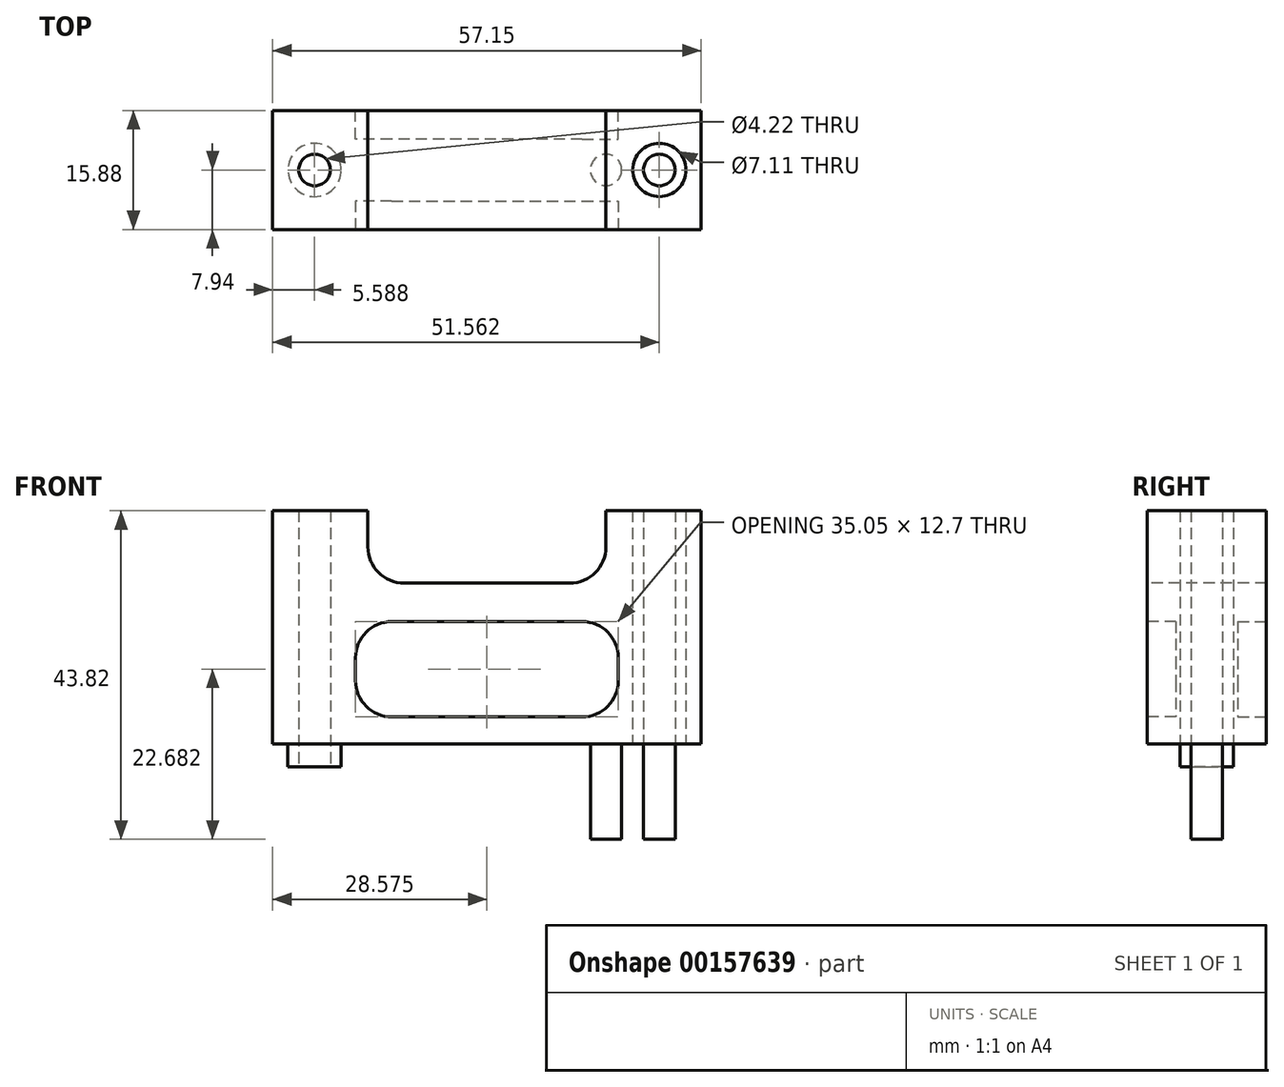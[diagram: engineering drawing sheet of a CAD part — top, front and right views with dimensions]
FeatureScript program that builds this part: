
annotation { "Feature Type Name" : "Feature", "Feature Type Description" : "" }
export const myFeature = defineFeature(function(context is Context, id is Id, definition is map)
    precondition{}
    {
        {
            var Q0;
            Q0=qCreatedBy(makeId("Right.planeOp"),FACE);
            var sketch = newSketch(context, id + "F0", { "sketchPlane" : qUnion([Q0])});
            skLineSegment(sketch, "E0", {"start": v(0, 0) * mm, "end": v(0, 11.18) * mm});
            skLineSegment(sketch, "E1", {"start": v(0, 11.18) * mm, "end": v(4.76, 11.18) * mm});
            skLineSegment(sketch, "E2", {"start": v(4.76, 11.18) * mm, "end": v(4.76, 43.82) * mm});
            skLineSegment(sketch, "E3", {"start": v(4.76, 43.82) * mm, "end": v(20.64, 43.82) * mm});
            skLineSegment(sketch, "E4", {"start": v(20.64, 43.82) * mm, "end": v(20.64, 11.18) * mm});
            skLineSegment(sketch, "E5", {"start": v(20.64, 11.18) * mm, "end": v(25.4, 11.18) * mm});
            skLineSegment(sketch, "E6", {"start": v(25.4, 11.18) * mm, "end": v(25.4, 0) * mm});
            skLineSegment(sketch, "E7", {"start": v(25.4, 0) * mm, "end": v(0, 0) * mm});
            skSolve(sketch);
        }
        {
            var Q0;
            Q0=makeQuery(id+"F0.imprint","IMPRINT",FACE,{"disambiguationData":[TD([[makeQuery(id+"F0.imprint","IMPRINT",EDGE,{"derivedFrom":sQuery(id+"F0.wireOp",EDGE,"E0")}),-1.0]])]});
            extrude(context, id + "F1", {"entities" : qUnion([Q0]), "oppositeDirection" : true, "depth" : 57.15 * mm});
        }
        {
            var Q0;
            Q0=makeQuery(id+"F1.opExtrude","SWEPT_FACE",FACE,{"disambiguationData":[OSD([sQuery(id+"F0.wireOp",EDGE,"E2")])]});
            var sketch = newSketch(context, id + "F2", { "sketchPlane" : qUnion([Q0])});
            skLineSegment(sketch, "E8", {"start": v(-44.45, 43.82) * mm, "end": v(-44.45, 38.99) * mm});
            skLineSegment(sketch, "E9", {"start": v(-39.62, 34.16) * mm, "end": v(-17.53, 34.16) * mm});
            skLineSegment(sketch, "E10", {"start": v(-12.7, 38.99) * mm, "end": v(-12.7, 43.82) * mm});
            skPoint(sketch, "E11.visualSharp", {"position": v(-44.45, 34.16) * mm});
            skArc(sketch, "E11.filletArc", {"start": v(-44.45, 38.99) * mm, "mid": v(-43.04, 35.58) * mm, "end": v(-39.62, 34.16) * mm});
            skPoint(sketch, "E12.visualSharp", {"position": v(-12.7, 34.16) * mm});
            skArc(sketch, "E12.filletArc", {"start": v(-17.53, 34.16) * mm, "mid": v(-14.11, 35.58) * mm, "end": v(-12.7, 38.99) * mm});
            skSolve(sketch);
        }
        {
            var Q0;
            {var subQ1=sQuery(id+"F2.wireOp",EDGE,"E8");Q0=makeQuery(id+"F2.imprint","IMPRINT",FACE,{"disambiguationData":[TD([[makeQuery(id+"F2.imprint","IMPRINT",EDGE,{"derivedFrom":subQ1}),1.0]])]});}
            extrude(context, id + "F3", {"entities" : qUnion([Q0]), "operationType" : NewBodyOperationType.REMOVE, "oppositeDirection" : true, "depth" : 25.4 * mm});
        }
        {
            var Q0;
            Q0=makeQuery(id+"F1.opExtrude","SWEPT_FACE",FACE,{"disambiguationData":[OSD([sQuery(id+"F0.wireOp",EDGE,"E2")])]});
            var sketch = newSketch(context, id + "F4", { "sketchPlane" : qUnion([Q0])});
            skLineSegment(sketch, "E13.bottom", {"start": v(-41.28, 29.03) * mm, "end": v(-15.88, 29.03) * mm});
            skLineSegment(sketch, "E13.top", {"start": v(-41.28, 16.33) * mm, "end": v(-15.88, 16.33) * mm});
            skLineSegment(sketch, "E13.left", {"start": v(-46.1, 24.2) * mm, "end": v(-46.1, 21.16) * mm});
            skLineSegment(sketch, "E13.right", {"start": v(-11.05, 24.2) * mm, "end": v(-11.05, 21.16) * mm});
            skPoint(sketch, "E14.end.orphan", {"position": v(0, 17.14) * mm});
            skPoint(sketch, "E15.visualSharp", {"position": v(-46.1, 16.33) * mm});
            skArc(sketch, "E15.filletArc", {"start": v(-46.1, 21.16) * mm, "mid": v(-44.69, 17.75) * mm, "end": v(-41.28, 16.33) * mm});
            skPoint(sketch, "E16.visualSharp", {"position": v(-46.1, 29.03) * mm});
            skArc(sketch, "E16.filletArc", {"start": v(-41.28, 29.03) * mm, "mid": v(-44.69, 27.62) * mm, "end": v(-46.1, 24.2) * mm});
            skPoint(sketch, "E17.visualSharp", {"position": v(-11.05, 29.03) * mm});
            skArc(sketch, "E17.filletArc", {"start": v(-11.05, 24.2) * mm, "mid": v(-12.46, 27.62) * mm, "end": v(-15.88, 29.03) * mm});
            skPoint(sketch, "E18.visualSharp", {"position": v(-11.05, 16.33) * mm});
            skArc(sketch, "E18.filletArc", {"start": v(-15.88, 16.33) * mm, "mid": v(-12.46, 17.75) * mm, "end": v(-11.05, 21.16) * mm});
            skSolve(sketch);
        }
        {
            var Q0;
            Q0=makeQuery(id+"F4.imprint","IMPRINT",FACE,{"disambiguationData":[TD([[makeQuery(id+"F4.imprint","IMPRINT",EDGE,{"derivedFrom":sQuery(id+"F4.wireOp",EDGE,"E13.bottom")}),-1.0]])]});
            extrude(context, id + "F5", {"entities" : qUnion([Q0]), "operationType" : NewBodyOperationType.REMOVE, "oppositeDirection" : true, "depth" : 3.8 * mm});
        }
        {
            var Q0;
            Q0=makeQuery(id+"F1.opExtrude","SWEPT_FACE",FACE,{"disambiguationData":[OSD([sQuery(id+"F0.wireOp",EDGE,"E4")])]});
            var sketch = newSketch(context, id + "F6", { "sketchPlane" : qUnion([Q0])});
            skLineSegment(sketch, "E19.bottom", {"start": v(15.88, 29.03) * mm, "end": v(41.27, 29.03) * mm});
            skLineSegment(sketch, "E19.top", {"start": v(15.88, 16.33) * mm, "end": v(41.28, 16.33) * mm});
            skLineSegment(sketch, "E19.left", {"start": v(11.05, 24.2) * mm, "end": v(11.05, 21.16) * mm});
            skLineSegment(sketch, "E19.right", {"start": v(46.1, 24.2) * mm, "end": v(46.1, 21.16) * mm});
            skPoint(sketch, "E20.end.orphan", {"position": v(54.95, 20.19) * mm});
            skPoint(sketch, "E21.visualSharp", {"position": v(11.05, 16.33) * mm});
            skArc(sketch, "E21.filletArc", {"start": v(11.05, 21.16) * mm, "mid": v(12.46, 17.75) * mm, "end": v(15.88, 16.33) * mm});
            skPoint(sketch, "E22.visualSharp", {"position": v(11.05, 29.03) * mm});
            skArc(sketch, "E22.filletArc", {"start": v(15.88, 29.03) * mm, "mid": v(12.46, 27.62) * mm, "end": v(11.05, 24.2) * mm});
            skPoint(sketch, "E23.visualSharp", {"position": v(46.1, 29.03) * mm});
            skArc(sketch, "E23.filletArc", {"start": v(46.1, 24.2) * mm, "mid": v(44.69, 27.62) * mm, "end": v(41.27, 29.03) * mm});
            skPoint(sketch, "E24.visualSharp", {"position": v(46.1, 16.33) * mm});
            skArc(sketch, "E24.filletArc", {"start": v(41.28, 16.33) * mm, "mid": v(44.69, 17.75) * mm, "end": v(46.1, 21.16) * mm});
            skLineSegment(sketch, "E25", {"start": v(23.32, 16.33) * mm, "end": v(23.32, 11.18) * mm, "construction": true});
            skLineSegment(sketch, "E26", {"start": v(46.1, 21.16) * mm, "end": v(57.15, 21.16) * mm, "construction": true});
            skLineSegment(sketch, "E27", {"start": v(11.05, 21.16) * mm, "end": v(0, 21.16) * mm, "construction": true});
            skSolve(sketch);
        }
        {
            var Q0;
            Q0=makeQuery(id+"F6.imprint","IMPRINT",FACE,{"disambiguationData":[TD([[makeQuery(id+"F6.imprint","IMPRINT",EDGE,{"derivedFrom":sQuery(id+"F6.wireOp",EDGE,"E19.bottom")}),-1.0]])]});
            extrude(context, id + "F7", {"entities" : qUnion([Q0]), "operationType" : NewBodyOperationType.REMOVE, "oppositeDirection" : true, "depth" : 3.8 * mm});
        }
        {
            var Q0;
            Q0=makeQuery(id+"F1.opExtrude","SWEPT_FACE",FACE,{"disambiguationData":[OSD([sQuery(id+"F0.wireOp",EDGE,"E7")])]});
            var sketch = newSketch(context, id + "F8", { "sketchPlane" : qUnion([Q0])});
            skLineSegment(sketch, "E28", {"start": v(-28.58, 0) * mm, "end": v(-28.58, -25.4) * mm, "construction": true});
            skCircle(sketch, "E29", {"center": v(-51.56, -12.7) * mm, "radius": 2.1 * mm});
            skPoint(sketch, "E29.centerSnap0", {"position": v(-57.15, -12.7) * mm});
            skCircle(sketch, "E30", {"center": v(-51.56, -12.7) * mm, "radius": 3.56 * mm});
            skCircle(sketch, "E31", {"center": v(-44.45, -12.7) * mm, "radius": 2.08 * mm});
            skCircle(sketch, "E32.MirrorC", {"center": v(-12.7, -12.7) * mm, "radius": 2.08 * mm});
            skCircle(sketch, "E33.MirrorC", {"center": v(-5.59, -12.7) * mm, "radius": 3.56 * mm});
            skCircle(sketch, "E34.MirrorC", {"center": v(-5.59, -12.7) * mm, "radius": 2.1 * mm});
            skSolve(sketch);
        }
        {
            var Q0;
            Q0=makeQuery(id+"F8.imprint","IMPRINT",FACE,{"disambiguationData":[TD([[makeQuery(id+"F8.imprint","IMPRINT",EDGE,{"derivedFrom":sQuery(id+"F8.wireOp",EDGE,"E31")}),1.0]])]});
            var Q1;
            Q1=makeQuery(id+"F8.imprint","IMPRINT",FACE,{"disambiguationData":[TD([[makeQuery(id+"F8.imprint","IMPRINT",EDGE,{"derivedFrom":sQuery(id+"F8.wireOp",EDGE,"E32.MirrorC")}),-1.0]])]});
            extrude(context, id + "F9", {"entities" : qUnion([Q0, Q1]), "operationType" : NewBodyOperationType.REMOVE, "oppositeDirection" : true, "depth" : 12.7 * mm});
        }
        {
            var Q0;
            Q0=makeQuery(id+"F8.imprint","IMPRINT",FACE,{"disambiguationData":[TD([[makeQuery(id+"F8.imprint","IMPRINT",EDGE,{"derivedFrom":sQuery(id+"F8.wireOp",EDGE,"E29")}),1.0]])]});
            var Q1;
            Q1=makeQuery(id+"F8.imprint","IMPRINT",FACE,{"disambiguationData":[TD([[makeQuery(id+"F8.imprint","IMPRINT",EDGE,{"derivedFrom":sQuery(id+"F8.wireOp",EDGE,"E34.MirrorC")}),-1.0]])]});
            extrude(context, id + "F10", {"entities" : qUnion([Q0, Q1]), "operationType" : NewBodyOperationType.REMOVE, "endBound" : BoundingType.THROUGH_ALL, "oppositeDirection" : true, "depth" : 25.4 * mm});
        }
        {
            var Q0;
            Q0=makeQuery(id+"F8.imprint","IMPRINT",FACE,{"disambiguationData":[TD([[makeQuery(id+"F8.imprint","IMPRINT",EDGE,{"derivedFrom":sQuery(id+"F8.wireOp",EDGE,"E29")}),-1.0]])]});
            var Q1;
            Q1=makeQuery(id+"F8.imprint","IMPRINT",FACE,{"disambiguationData":[TD([[makeQuery(id+"F8.imprint","IMPRINT",EDGE,{"derivedFrom":sQuery(id+"F8.wireOp",EDGE,"E33.MirrorC")}),-1.0]])]});
            extrude(context, id + "F11", {"entities" : qUnion([Q0, Q1]), "operationType" : NewBodyOperationType.REMOVE, "oppositeDirection" : true, "depth" : 9.65 * mm});
        }
    });
